# Revit family: PRD_FrankeWS_UtltSpplCntrlPnls_EXOSWCController_EXOS0027
name_source: partatom
category: Electrical Fixtures
revit_build: Autodesk Revit 2018 (Build: 20190510_1515(x64)
units: mm (PartAtom-declared; Revit-internal decimal feet)

## family parameters
Cut with Voids When Loaded = No
Host = Face
Maintain Annotation Orientation = No
OmniClass Number = 23.45.05.14.99
OmniClass Title = Other Sanitary Washing Plumbing Fixtures
Part Type = Normal
Room Calculation Point = No
Round Connector Dimension = Use Diameter
Shared = No

## types (1)
- EXOS0027
    ApparentLoad = 0 VA
    AssetType = Fixed
    BIMObjectName = PRD_AR_UtilitySupplyControlPanels_EXOSWCController_EXOS0027
    CasingMaterial = PRD_AR_StainlessSteel_Brushed
    Category = Pr_75_50_18_93, Utility supply control panels
    Default Elevation = 1000 mm  [stored 3.28084 ft]
    DefaultAutomaticHygieneFlushing = 24h after the last activity
    Description = EXOS - A3000 open opto-electronic WC control for concealed toilet cistern. With option for external controlling options such as fittings settings and communication via ECC function controller or optional, bidirectional remote control. With waterproof electronic module with additional input for sensors to be provided by the client no more than 5 m away (e.g. support grips for disabled persons), low voltage motor, waterproof electric T-junction for connecting to system cable, mounting bracket and stainless steel cover plate with sensors and concealed screw fastening. Activated water hygiene flushing 24 hours after last activation and saving of statistical data. Separate power supply 24 V DC via AQUA 3000 open system accessories.
    DurationUnit = year
    Features = mounting bracket and stainless steel cover plate with sensors and concealed screw fastening
    Finish = Brushed
    FunctionalPrinciple = Electronic self-closing
    GrossWeight = 1.25 kg
    IfcExportAs = IfcControllerType
    IfcExportType = USERDEFINED
    MainColor = stainless steel
    Manufacturer = KWC Group AG
    ManufacturerName = KWC Group AG
    ManufacturerURL = www.kwc.com
    Material = Stainless steel
    MaterialCasing = Stainless steel
    MaterialCodeCasing = 1.4301 Chrome Nickel steel V2A
    MaterialFitting = Synthetic
    Model = EXOS0027
    ModelNumber = 2030036621
    ModelReference = EXOS0027
    Name = EXOS WC controller for cistern EXOS0027
    NetWeight = 1.20 kg
    NominalDepth = 0 mm  [stored 0 ft]
    NominalHeight = 147 mm  [stored 0.482283 ft]
    NominalWidth = 207 mm  [stored 0.679134 ft]
    PowerConsumption = 4
    PowerFactor = 1
    PowerSupplyConnection = 24 V DC
    ProductCode = 209.0599.857
    ProductInformation = https://pim.kwc.com
    ProtectiveSystemIP = 68
    Status = New
    SurfaceFinishCasing = Brushed
    TypeOfFlushingFitting = For WC cistern
    TypeOfOperation = Sensor operation
    TypeOfSensor = Opto-electronic sensor
    URL = www.kwc.com
    Uniclass2015Code = Pr_75_50_18_93
    Uniclass2015Title = Utility supply control panels
    Uniclass2015Version = Products v1.17
    Version = 1
    Voltage = 0 V
    WarrantyDurationUnit = year

note: [stored X ft] marks values corroborated as IEEE doubles in the binary element streams (Revit-internal decimal feet)

## geometry (parser evidence)
native form markers: Sweep x2
no freeform markers — native parametric forms only
